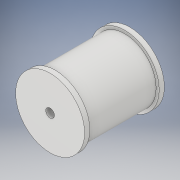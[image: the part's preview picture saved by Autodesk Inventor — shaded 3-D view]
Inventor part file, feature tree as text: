
AUTODESK INVENTOR PART (.ipt)
format: ipt  version: 2019 (Build 230136000, 136)  size: 120,832 bytes
history: native  units: mm
features: sketch x4, extrude x3, other x1, hole x1
ambient origin geometry x8: Origin, YZ Plane, XZ Plane, XY Plane, X Axis, Y Axis, Z Axis, Center Point
bodies: Body1 (feature_tree)
feature tree (9):
  other  "ソリッド1"
  extrude  "押し出し1"  Depth=36.26mm
  extrude  "押し出し2"  Depth=40.0mm TaperAngle=0.0deg
  extrude  "押し出し3"  Depth=39.76mm
  hole  "穴1"  [1 undecoded]
  sketch  "スケッチ1"
  sketch  "スケッチ2"
  sketch  "スケッチ3"
  sketch  "スケッチ4"
note: 1 required parameter value undecoded (feature->parameter linkage not recoverable at this tier; creation-order binding heuristic only, values carry confidence <= 0.55)
